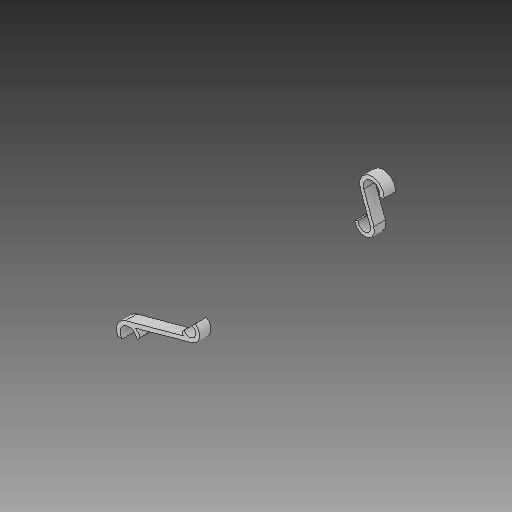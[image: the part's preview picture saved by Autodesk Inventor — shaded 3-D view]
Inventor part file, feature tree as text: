
AUTODESK INVENTOR PART (.ipt)
format: ipt  version: 2019.3 (Build 233278000, 278)  size: 143,360 bytes
history: native  units: mm
features: other x7, sketch x2, extrude x2, reference x2
ambient origin geometry x8: Origin, YZ Plane, XZ Plane, XY Plane, X Axis, Y Axis, Z Axis, Center Point
bodies: Body1 (feature_tree), Body2 (feature_tree)
feature tree (13):
  other  "HolderBottom"
  sketch  "Sketch1"  dims[d0=5.0mm d1=5.0mm d6=5.0mm d7=5.0mm]
  sketch  "Sketch2"  dims[d8=15.0mm d9=0.0mm d10=15.0mm d11=0.0mm]
  extrude  "Extrusion2"  Depth=5.0mm
  extrude  "Extrusion3"  Depth=15.0mm TaperAngle=0.0deg
  reference  "Reference1"
  reference  "Reference2"
  other  "HolderUpper"
  other  "<userpath>\Desktop\3dprojects\OpenEmoto\MainFrame\Battery\LowerCageJig\HolderAssembly.iam"
  other  "HolderAssembly.iam"
  other  "Assembly:1"
  other  "LowerCage:1"
  other  "MainFrame:1"
